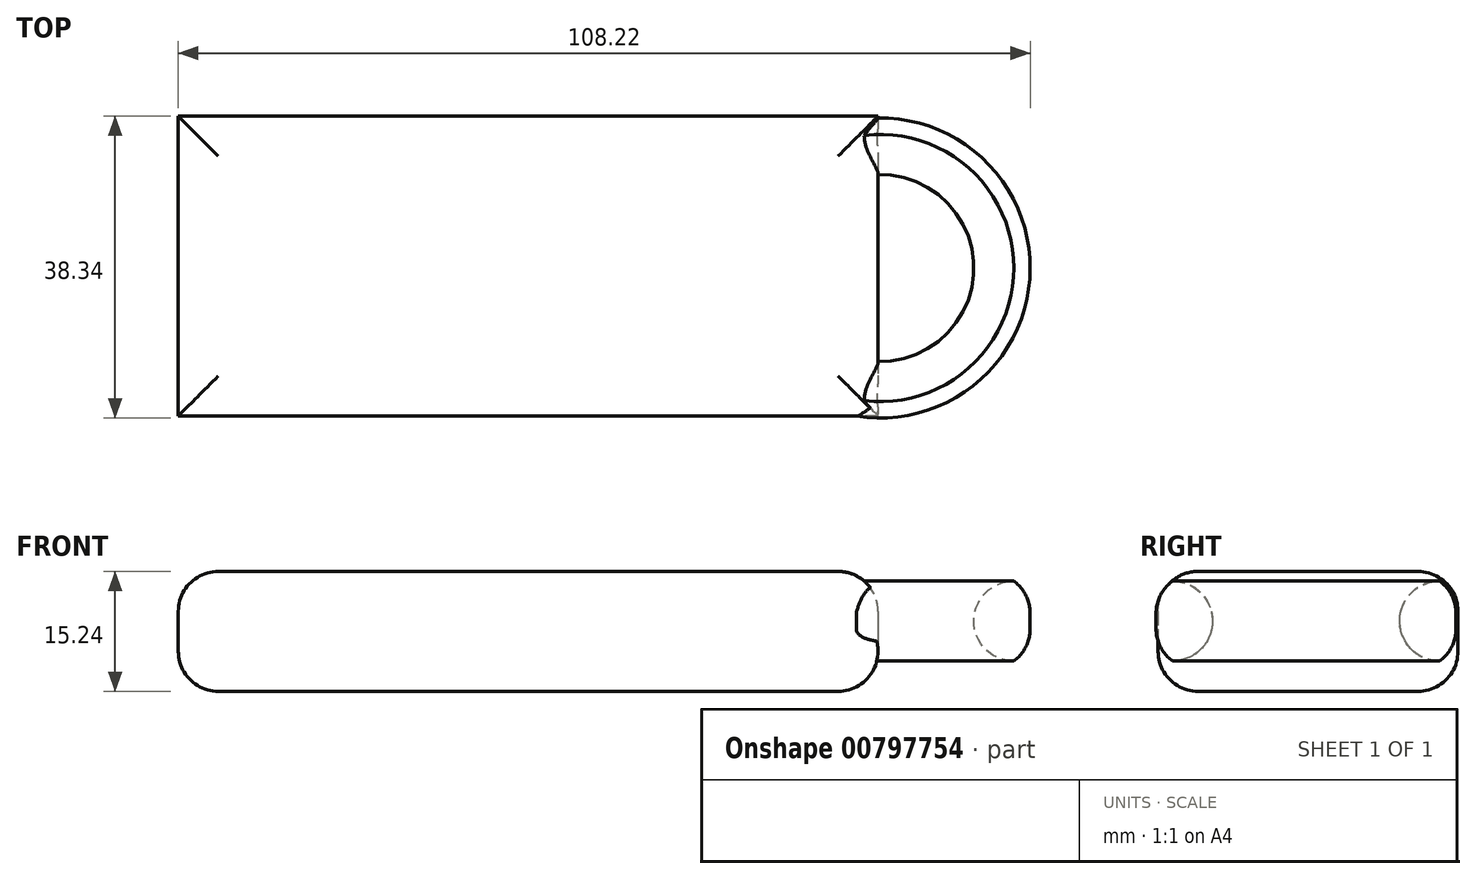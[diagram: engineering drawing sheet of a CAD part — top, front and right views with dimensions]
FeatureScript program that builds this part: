
annotation { "Feature Type Name" : "Feature", "Feature Type Description" : "" }
export const myFeature = defineFeature(function(context is Context, id is Id, definition is map)
    precondition{}
    {
        {
            var Q0;
            Q0=qCreatedBy(makeId("Front.planeOp"),FACE);
            var sketch = newSketch(context, id + "F0", { "sketchPlane" : qUnion([Q0])});
            skLineSegment(sketch, "E0.bottom", {"start": v(-60.56, 11.4) * mm, "end": v(28.34, 11.4) * mm});
            skLineSegment(sketch, "E0.top", {"start": v(-60.56, -3.85) * mm, "end": v(28.34, -3.85) * mm});
            skLineSegment(sketch, "E0.left", {"start": v(-60.56, 11.4) * mm, "end": v(-60.56, -3.85) * mm});
            skLineSegment(sketch, "E0.right", {"start": v(28.34, 11.4) * mm, "end": v(28.34, -3.85) * mm});
            skSolve(sketch);
        }
        {
            var Q0;
            Q0 = qSketchRegion(id + "F0", true);
            extrude(context, id + "F1", {"entities" : qUnion([Q0]), "oppositeDirection" : true, "depth" : 38.1 * mm, "offsetDistance" : 25.4 * mm});
        }
        {
            var Q0;
            Q0=qCreatedBy(makeId("Top.planeOp"),FACE);
            var sketch = newSketch(context, id + "F2", { "sketchPlane" : qUnion([Q0])});
            skCircle(sketch, "E1", {"center": v(28.6, 18.8) * mm, "radius": 19.05 * mm});
            skCircle(sketch, "E2", {"center": v(28.6, 18.8) * mm, "radius": 11.89 * mm});
            skSolve(sketch);
        }
        {
            var Q0;
            Q0=makeQuery(id+"F2.imprint","IMPRINT",FACE,{"disambiguationData":[TD([[makeQuery(id+"F2.imprint","IMPRINT",EDGE,{"derivedFrom":sQuery(id+"F2.wireOp",EDGE,"E1")}),1.0]])]});
            extrude(context, id + "F3", {"entities" : qUnion([Q0]), "operationType" : NewBodyOperationType.ADD, "depth" : 10.16 * mm, "offsetDistance" : 25.4 * mm});
        }
        {
            var Q0;
            Q0=makeQuery(id+"F1.opExtrude","SWEPT_FACE",FACE,{"disambiguationData":[OSD([sQuery(id+"F0.wireOp",EDGE,"E0.bottom")])]});
            fillet(context, id + "F4", {"entities" : qUnion([Q0]), "radius" : 5.08 * mm, "tangentPropagation" : true, "allowEdgeOverflow" : false});
        }
        {
            var Q0;
            Q0=makeQuery(id+"F1.opExtrude","SWEPT_FACE",FACE,{"disambiguationData":[OSD([sQuery(id+"F0.wireOp",EDGE,"E0.top")])]});
            fillet(context, id + "F5", {"entities" : qUnion([Q0]), "radius" : 5.08 * mm, "tangentPropagation" : true, "allowEdgeOverflow" : false});
        }
        {
            var Q0;
            Q0=makeQuery(id+"F3.opExtrude","CAP_EDGE",EDGE,{"disambiguationData":[OSD([sQuery(id+"F2.wireOp",EDGE,"E2")])],"isStart":true});
            fillet(context, id + "F6", {"entities" : qUnion([Q0]), "radius" : 5.08 * mm, "tangentPropagation" : true, "allowEdgeOverflow" : false});
        }
        {
            var Q0;
            Q0=makeQuery(id+"F3.opExtrude","CAP_EDGE",EDGE,{"disambiguationData":[OSD([sQuery(id+"F2.wireOp",EDGE,"E1")])],"isStart":true});
            fillet(context, id + "F7", {"entities" : qUnion([Q0]), "radius" : 5.08 * mm, "tangentPropagation" : true, "allowEdgeOverflow" : false});
        }
        {
            var Q0;
            Q0=makeQuery(id+"F3.opExtrude","CAP_EDGE",EDGE,{"disambiguationData":[OSD([sQuery(id+"F2.wireOp",EDGE,"E2")])],"isStart":false});
            fillet(context, id + "F8", {"entities" : qUnion([Q0]), "radius" : 5.08 * mm, "tangentPropagation" : true, "allowEdgeOverflow" : false});
        }
        {
            var Q0;
            Q0=makeQuery(id+"F3.opExtrude","CAP_EDGE",EDGE,{"disambiguationData":[OSD([sQuery(id+"F2.wireOp",EDGE,"E1")])],"isStart":false});
            fillet(context, id + "F9", {"entities" : qUnion([Q0]), "radius" : 5.08 * mm, "tangentPropagation" : true, "allowEdgeOverflow" : false});
        }
    });
